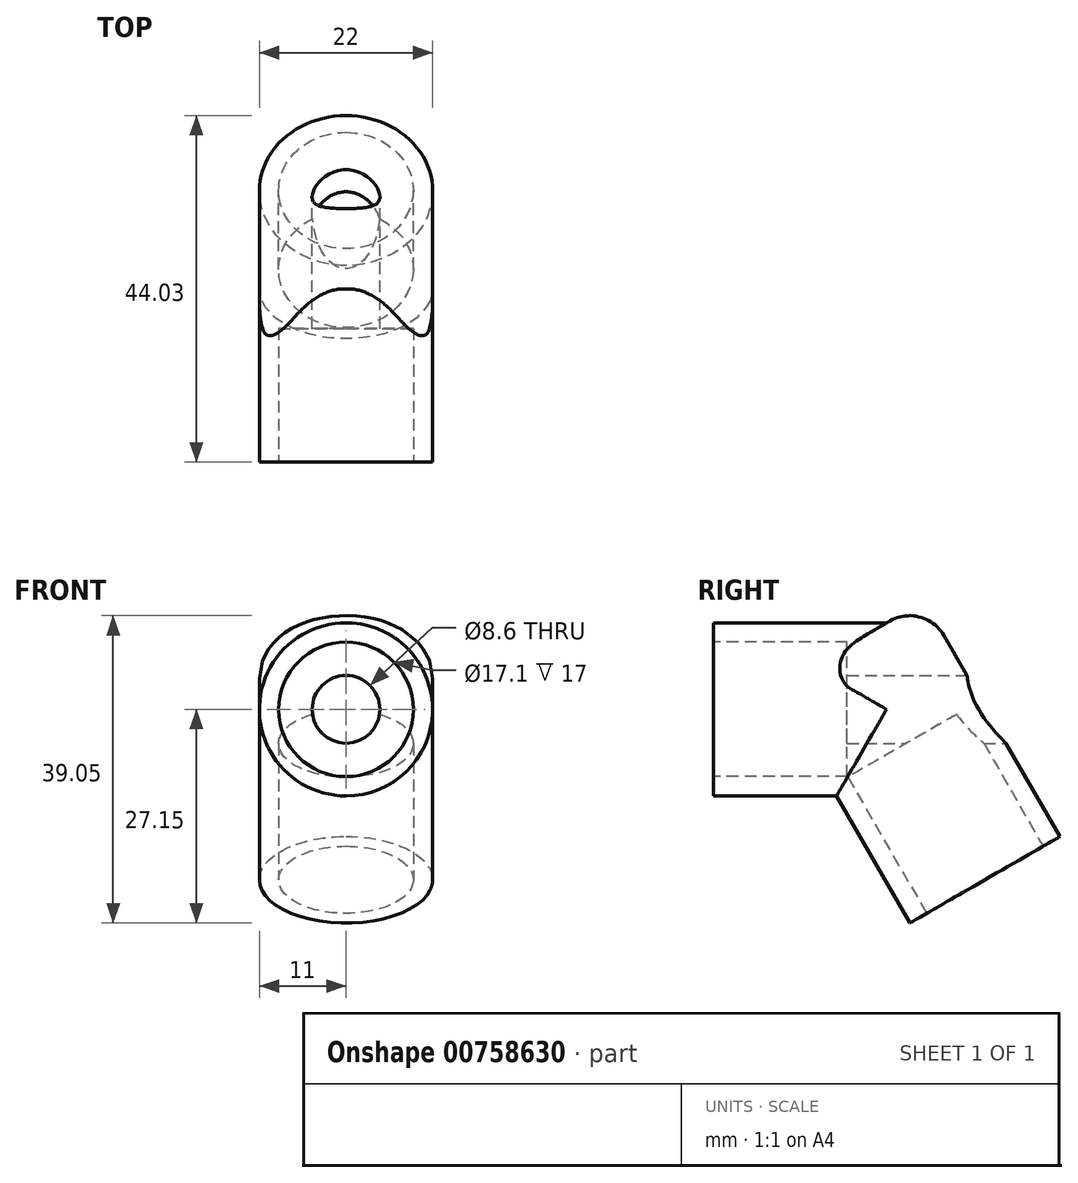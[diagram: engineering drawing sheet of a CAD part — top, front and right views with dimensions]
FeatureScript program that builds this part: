
annotation { "Feature Type Name" : "Feature", "Feature Type Description" : "" }
export const myFeature = defineFeature(function(context is Context, id is Id, definition is map)
    precondition{}
    {
        {
            var Q0;
            Q0=qCreatedBy(makeId("Front.planeOp"),FACE);
            var sketch = newSketch(context, id + "F0", { "sketchPlane" : qUnion([Q0])});
            skCircle(sketch, "E0", {"center": v(0, 0) * mm, "radius": 11 * mm});
            skSolve(sketch);
        }
        {
            var Q0;
            Q0=makeQuery(id+"F0.imprint","IMPRINT",FACE,{"disambiguationData":[TD([[makeQuery(id+"F0.imprint","IMPRINT",EDGE,{"derivedFrom":sQuery(id+"F0.wireOp",EDGE,"E0")}),1.0]])]});
            extrude(context, id + "F1", {"entities" : qUnion([Q0]), "depth" : 22 * mm, "offsetDistance" : 25 * mm});
        }
        {
            var Q0;
            Q0=qCreatedBy(makeId("Front.planeOp"),FACE);
            var sketch = newSketch(context, id + "F2", { "sketchPlane" : qUnion([Q0])});
            skLineSegment(sketch, "E1", {"start": v(34.53, 0) * mm, "end": v(-34.53, 0) * mm});
            skSolve(sketch);
        }
        {
            var Q0;
            Q0=qCreatedBy(makeId("Top.planeOp"),FACE);
            var Q1;
            Q1=sQuery(id+"F2.wireOp",EDGE,"E1");
            cPlane(context, id + "F3", {"entities" : qUnion([Q0, Q1]), "cplaneType" : CPlaneType.LINE_ANGLE, "offset" : 25 * mm, "angle" : 30 * degree, "oppositeDirection" : true, "width" : 150 * mm, "height" : 150 * mm});
        }
        {
            var Q0;
            Q0=qCreatedBy(id+"F3.planeOp",FACE);
            var sketch = newSketch(context, id + "F4", { "sketchPlane" : qUnion([Q0])});
            skCircle(sketch, "E2", {"center": v(0, 0) * mm, "radius": 11 * mm});
            skSolve(sketch);
        }
        {
            var Q0;
            Q0 = qSketchRegion(id + "F4", true);
            extrude(context, id + "F5", {"entities" : qUnion([Q0]), "operationType" : NewBodyOperationType.ADD, "depth" : 25 * mm, "offsetDistance" : 25 * mm, "hasSecondDirection" : true, "secondDirectionOppositeDirection" : true, "secondDirectionDepth" : 9.5 * mm});
        }
        {
            var Q0;
            Q0=makeQuery(id+"F5.opExtrude","CAP_FACE",FACE,{"disambiguationData":[OSD([sQuery(id+"F4.wireOp",EDGE,"E2")])],"isStart":false});
            var sketch = newSketch(context, id + "F6", { "sketchPlane" : qUnion([Q0])});
            skCircle(sketch, "E3", {"center": v(0, 0) * mm, "radius": 8.55 * mm});
            skSolve(sketch);
        }
        {
            var Q0;
            Q0=makeQuery(id+"F6.imprint","IMPRINT",FACE,{"disambiguationData":[TD([[makeQuery(id+"F6.imprint","IMPRINT",EDGE,{"derivedFrom":sQuery(id+"F6.wireOp",EDGE,"E3")}),1.0]])]});
            extrude(context, id + "F7", {"entities" : qUnion([Q0]), "operationType" : NewBodyOperationType.REMOVE, "oppositeDirection" : true, "depth" : 20 * mm, "offsetDistance" : 25 * mm});
        }
        {
            var Q0;
            Q0=makeQuery(id+"F1.opExtrude","CAP_FACE",FACE,{"disambiguationData":[OSD([sQuery(id+"F0.wireOp",EDGE,"E0")])],"isStart":true});
            var sketch = newSketch(context, id + "F8", { "sketchPlane" : qUnion([Q0])});
            skCircle(sketch, "E4", {"center": v(0, 0) * mm, "radius": 4.3 * mm});
            skSolve(sketch);
        }
        {
            var Q0;
            Q0=makeQuery(id+"F8.imprint","IMPRINT",FACE,{"disambiguationData":[TD([[makeQuery(id+"F8.imprint","IMPRINT",EDGE,{"derivedFrom":sQuery(id+"F8.wireOp",EDGE,"E4")}),1.0]])]});
            extrude(context, id + "F9", {"entities" : qUnion([Q0]), "operationType" : NewBodyOperationType.REMOVE, "endBound" : BoundingType.UP_TO_NEXT, "oppositeDirection" : true, "depth" : 17 * mm, "offsetDistance" : 25 * mm, "hasSecondDirection" : true, "secondDirectionBound" : BoundingType.THROUGH_ALL, "secondDirectionOppositeDirection" : false, "secondDirectionDepth" : 25 * mm});
        }
        {
            var Q0;
            Q0=makeQuery(id+"F1.opExtrude","CAP_FACE",FACE,{"disambiguationData":[OSD([sQuery(id+"F0.wireOp",EDGE,"E0")])],"isStart":false});
            var sketch = newSketch(context, id + "F10", { "sketchPlane" : qUnion([Q0])});
            skCircle(sketch, "E5", {"center": v(0, 0) * mm, "radius": 8.55 * mm});
            skSolve(sketch);
        }
        {
            var Q0;
            Q0=makeQuery(id+"F10.imprint","IMPRINT",FACE,{"disambiguationData":[TD([[makeQuery(id+"F10.imprint","IMPRINT",EDGE,{"derivedFrom":sQuery(id+"F10.wireOp",EDGE,"E5")}),1.0]])]});
            var Q1;
            Q1=sQuery(id+"F10.wireOp",EDGE,"E5");
            extrude(context, id + "F11", {"entities" : qUnion([Q0]), "operationType" : NewBodyOperationType.REMOVE, "surfaceEntities" : qUnion([Q1]), "oppositeDirection" : true, "depth" : 17 * mm, "offsetDistance" : 25 * mm});
        }
        {
            var Q0;
            Q0=makeQuery(id+"F5.opExtrude","CAP_EDGE",EDGE,{"disambiguationData":[OSD([sQuery(id+"F4.wireOp",EDGE,"E2")])],"isStart":true});
            fillet(context, id + "F12", {"entities" : qUnion([Q0]), "radius" : 5 * mm, "tangentPropagation" : true, "allowEdgeOverflow" : false});
        }
    });
